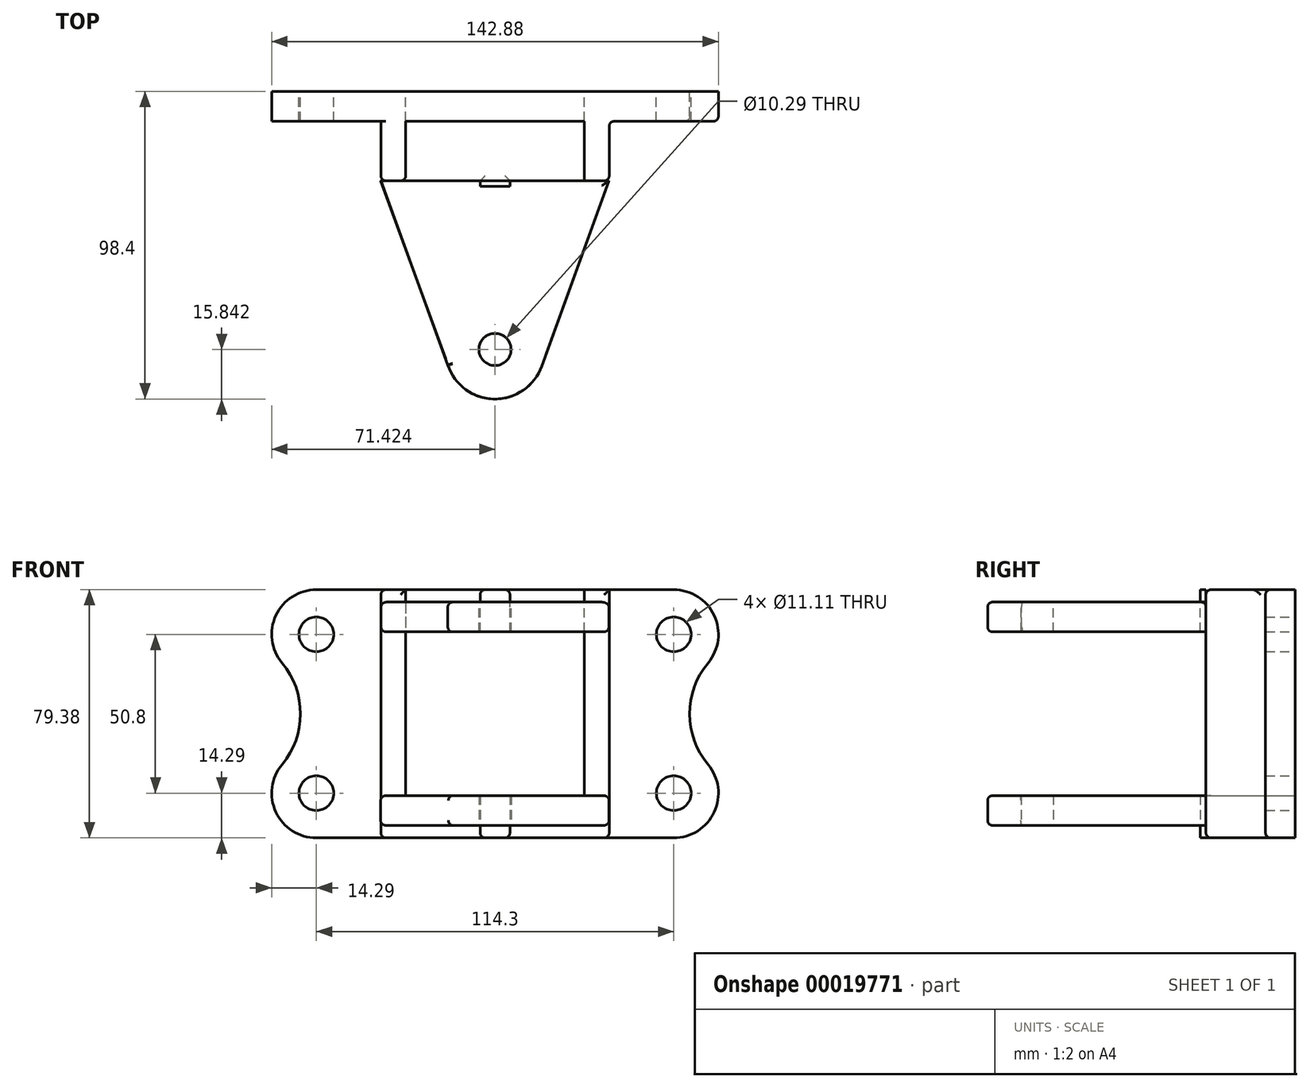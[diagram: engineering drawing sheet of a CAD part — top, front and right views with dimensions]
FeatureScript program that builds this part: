
annotation { "Feature Type Name" : "Feature", "Feature Type Description" : "" }
export const myFeature = defineFeature(function(context is Context, id is Id, definition is map)
    precondition{}
    {
        {
            var Q0;
            Q0=qCreatedBy(makeId("Front.planeOp"),FACE);
            var sketch = newSketch(context, id + "F0", { "sketchPlane" : qUnion([Q0])});
            skLineSegment(sketch, "E0.bottom", {"start": v(16.24, 39.69) * mm, "end": v(73.39, 39.69) * mm});
            skLineSegment(sketch, "E0.top", {"start": v(16.24, -39.69) * mm, "end": v(73.39, -39.69) * mm});
            skLineSegment(sketch, "E1", {"start": v(73.39, 39.69) * mm, "end": v(73.39, 25.4) * mm});
            skArc(sketch, "E2", {"start": v(84.37, 16.26) * mm, "mid": v(86.33, 31.46) * mm, "end": v(73.39, 39.69) * mm});
            skLineSegment(sketch, "E3", {"start": v(73.39, -39.69) * mm, "end": v(73.39, -25.4) * mm});
            skArc(sketch, "E4", {"start": v(73.39, -39.69) * mm, "mid": v(86.33, -31.46) * mm, "end": v(84.37, -16.26) * mm});
            skArc(sketch, "E5", {"start": v(84.37, 16.26) * mm, "mid": v(78.48, 0) * mm, "end": v(84.37, -16.26) * mm});
            skLineSegment(sketch, "E6.trimOffspring", {"start": v(73.39, -11.11) * mm, "end": v(73.39, -39.69) * mm});
            skCircle(sketch, "E7", {"center": v(73.39, 25.4) * mm, "radius": 5.56 * mm});
            skCircle(sketch, "E8", {"center": v(73.39, -25.4) * mm, "radius": 5.56 * mm});
            skLineSegment(sketch, "E9", {"start": v(73.39, 39.69) * mm, "end": v(16.24, 39.69) * mm});
            skLineSegment(sketch, "E10", {"start": v(16.24, 39.69) * mm, "end": v(16.24, 26.2) * mm});
            skLineSegment(sketch, "E11.MirrorCS", {"start": v(-40.91, -39.69) * mm, "end": v(-40.91, -25.4) * mm});
            skLineSegment(sketch, "E12.MirrorCS", {"start": v(16.24, -39.69) * mm, "end": v(-40.91, -39.69) * mm});
            skLineSegment(sketch, "E13.MirrorCS", {"start": v(16.24, 39.69) * mm, "end": v(-40.91, 39.69) * mm});
            skArc(sketch, "E14.MirrorCS", {"start": v(-51.89, 16.26) * mm, "mid": v(-53.85, 31.46) * mm, "end": v(-40.91, 39.69) * mm});
            skLineSegment(sketch, "E15.MirrorCS", {"start": v(-40.91, 39.69) * mm, "end": v(16.24, 39.69) * mm});
            skCircle(sketch, "E16.MirrorC", {"center": v(-40.91, -25.4) * mm, "radius": 5.56 * mm});
            skCircle(sketch, "E17.MirrorC", {"center": v(-40.91, 25.4) * mm, "radius": 5.56 * mm});
            skLineSegment(sketch, "E18.MirrorCS", {"start": v(-40.91, -11.11) * mm, "end": v(-40.91, -39.69) * mm});
            skArc(sketch, "E19.MirrorCS", {"start": v(-51.89, 16.26) * mm, "mid": v(-46, 0) * mm, "end": v(-51.89, -16.26) * mm});
            skArc(sketch, "E20.MirrorCS", {"start": v(-40.91, -39.69) * mm, "mid": v(-53.85, -31.46) * mm, "end": v(-51.89, -16.26) * mm});
            skLineSegment(sketch, "E21.MirrorCS", {"start": v(-40.91, 39.69) * mm, "end": v(-40.91, 25.4) * mm});
            skLineSegment(sketch, "E22", {"start": v(16.24, 26.2) * mm, "end": v(-12.34, 26.2) * mm});
            skLineSegment(sketch, "E23", {"start": v(-12.34, 26.2) * mm, "end": v(-12.34, -26.2) * mm});
            skLineSegment(sketch, "E24", {"start": v(16.24, -26.2) * mm, "end": v(-12.34, -26.2) * mm});
            skLineSegment(sketch, "E25", {"start": v(16.24, -26.2) * mm, "end": v(44.81, -26.2) * mm});
            skLineSegment(sketch, "E26", {"start": v(44.81, -26.2) * mm, "end": v(44.81, 26.2) * mm});
            skLineSegment(sketch, "E27", {"start": v(44.81, 26.2) * mm, "end": v(16.24, 26.2) * mm});
            skPoint(sketch, "E28.end.orphan", {"position": v(-12.34, 0) * mm});
            skLineSegment(sketch, "E29.trimOffspring", {"start": v(16.24, -26.2) * mm, "end": v(16.24, -39.69) * mm});
            skPoint(sketch, "E30.end.orphan", {"position": v(44.81, 0) * mm});
            skPoint(sketch, "E31.start.orphan", {"position": v(16.24, 0) * mm});
            skSolve(sketch);
        }
        {
            var Q0;
            Q0=makeQuery(id+"F0.imprint","IMPRINT",FACE,{"disambiguationData":[TD([[makeQuery(id+"F0.imprint","IMPRINT",EDGE,{"derivedFrom":sQuery(id+"F0.wireOp",EDGE,"E10")}),-1.0]])]});
            var Q1;
            Q1=makeQuery(id+"F0.imprint","IMPRINT",FACE,{"disambiguationData":[TD([[makeQuery(id+"F0.imprint","IMPRINT",EDGE,{"derivedFrom":sQuery(id+"F0.wireOp",EDGE,"E0.top")}),1.0]])]});
            extrude(context, id + "F1", {"entities" : qUnion([Q0, Q1]), "depth" : 9.52 * mm});
        }
        {
            var Q0;
            Q0=makeQuery(id+"F1.opExtrude","CAP_FACE",FACE,{"disambiguationData":[OSD([sQuery(id+"F0.wireOp",EDGE,"E0.top"),sQuery(id+"F0.wireOp",EDGE,"E2"),sQuery(id+"F0.wireOp",EDGE,"E4"),sQuery(id+"F0.wireOp",EDGE,"E5"),sQuery(id+"F0.wireOp",EDGE,"E7"),sQuery(id+"F0.wireOp",EDGE,"E8"),sQuery(id+"F0.wireOp",EDGE,"E9"),sQuery(id+"F0.wireOp",EDGE,"E12.MirrorCS"),sQuery(id+"F0.wireOp",EDGE,"E14.MirrorCS"),sQuery(id+"F0.wireOp",EDGE,"E15.MirrorCS"),sQuery(id+"F0.wireOp",EDGE,"E16.MirrorC"),sQuery(id+"F0.wireOp",EDGE,"E17.MirrorC"),sQuery(id+"F0.wireOp",EDGE,"E19.MirrorCS"),sQuery(id+"F0.wireOp",EDGE,"E20.MirrorCS"),sQuery(id+"F0.wireOp",EDGE,"E22"),sQuery(id+"F0.wireOp",EDGE,"E23"),sQuery(id+"F0.wireOp",EDGE,"E24"),sQuery(id+"F0.wireOp",EDGE,"E25"),sQuery(id+"F0.wireOp",EDGE,"E26"),sQuery(id+"F0.wireOp",EDGE,"E27")])],"isStart":false});
            var sketch = newSketch(context, id + "F2", { "sketchPlane" : qUnion([Q0])});
            skLineSegment(sketch, "E32", {"start": v(-20.27, 39.69) * mm, "end": v(-20.27, -39.69) * mm});
            skLineSegment(sketch, "E33", {"start": v(-20.27, -39.69) * mm, "end": v(-12.34, -39.69) * mm});
            skLineSegment(sketch, "E34", {"start": v(-12.34, -39.69) * mm, "end": v(-12.34, 39.69) * mm});
            skLineSegment(sketch, "E35", {"start": v(-12.34, 39.69) * mm, "end": v(-20.27, 39.69) * mm});
            skLineSegment(sketch, "E36", {"start": v(44.81, 26.2) * mm, "end": v(44.81, 39.69) * mm});
            skLineSegment(sketch, "E37", {"start": v(44.81, 39.69) * mm, "end": v(44.81, -39.69) * mm});
            skLineSegment(sketch, "E38", {"start": v(44.81, -39.69) * mm, "end": v(52.75, -39.69) * mm});
            skLineSegment(sketch, "E39", {"start": v(52.75, -39.69) * mm, "end": v(52.75, 39.69) * mm});
            skLineSegment(sketch, "E40", {"start": v(52.75, 39.69) * mm, "end": v(44.81, 39.69) * mm});
            skLineSegment(sketch, "E41", {"start": v(-12.34, 39.69) * mm, "end": v(44.81, 39.69) * mm});
            skLineSegment(sketch, "E42", {"start": v(-12.34, 26.2) * mm, "end": v(44.81, 26.2) * mm});
            skLineSegment(sketch, "E43", {"start": v(-12.34, -26.2) * mm, "end": v(44.81, -26.2) * mm});
            skLineSegment(sketch, "E44", {"start": v(44.81, -26.2) * mm, "end": v(44.81, 26.2) * mm});
            skLineSegment(sketch, "E45", {"start": v(44.81, -39.69) * mm, "end": v(-12.34, -39.69) * mm});
            skSolve(sketch);
        }
        {
            var Q0;
            {var subQ1=sQuery(id+"F2.wireOp",EDGE,"E43");Q0=makeQuery(id+"F2.imprint","IMPRINT",FACE,{"disambiguationData":[TD([[makeQuery(id+"F2.imprint","IMPRINT",EDGE,{"derivedFrom":subQ1}),1.0]])]});}
            var Q1;
            Q1=makeQuery(id+"F2.imprint","IMPRINT",FACE,{"disambiguationData":[TD([[makeQuery(id+"F2.imprint","IMPRINT",EDGE,{"derivedFrom":sQuery(id+"F2.wireOp",EDGE,"E32")}),1.0]])]});
            var Q2;
            {var subQ2=sQuery(id+"F2.wireOp",EDGE,"E38");Q2=makeQuery(id+"F2.imprint","IMPRINT",FACE,{"disambiguationData":[TD([[makeQuery(id+"F2.imprint","IMPRINT",EDGE,{"derivedFrom":subQ2}),-1.0]])]});}
            var Q3;
            {var subQ1=sQuery(id+"F2.wireOp",EDGE,"E41");Q3=makeQuery(id+"F2.imprint","IMPRINT",FACE,{"disambiguationData":[TD([[makeQuery(id+"F2.imprint","IMPRINT",EDGE,{"derivedFrom":subQ1}),-1.0]])]});}
            extrude(context, id + "F3", {"entities" : qUnion([Q0, Q1, Q2, Q3]), "operationType" : NewBodyOperationType.ADD, "depth" : 19.05 * mm});
        }
        {
            var Q0;
            Q0=makeQuery(id+"F3.opExtrude","CAP_FACE",FACE,{"disambiguationData":[OSD([sQuery(id+"F2.wireOp",EDGE,"E32"),sQuery(id+"F2.wireOp",EDGE,"E33"),sQuery(id+"F2.wireOp",EDGE,"E34"),sQuery(id+"F2.wireOp",EDGE,"E35"),sQuery(id+"F2.wireOp",EDGE,"E38"),sQuery(id+"F2.wireOp",EDGE,"E39"),sQuery(id+"F2.wireOp",EDGE,"E40"),sQuery(id+"F2.wireOp",EDGE,"E41"),sQuery(id+"F2.wireOp",EDGE,"E42"),sQuery(id+"F2.wireOp",EDGE,"E43"),sQuery(id+"F2.wireOp",EDGE,"E44"),sQuery(id+"F2.wireOp",EDGE,"E45")])],"isStart":false});
            var sketch = newSketch(context, id + "F4", { "sketchPlane" : qUnion([Q0])});
            skLineSegment(sketch, "E46", {"start": v(16.24, -39.69) * mm, "end": v(21, -39.69) * mm});
            skLineSegment(sketch, "E47", {"start": v(16.24, -39.69) * mm, "end": v(11.48, -39.69) * mm});
            skLineSegment(sketch, "E48.bottom", {"start": v(11.48, -39.69) * mm, "end": v(21, -39.69) * mm});
            skLineSegment(sketch, "E48.top", {"start": v(11.48, -35.72) * mm, "end": v(21, -35.72) * mm});
            skLineSegment(sketch, "E48.left", {"start": v(11.48, -39.69) * mm, "end": v(11.48, -35.72) * mm});
            skLineSegment(sketch, "E48.right", {"start": v(21, -39.69) * mm, "end": v(21, -35.72) * mm});
            skLineSegment(sketch, "E49", {"start": v(11.48, 39.69) * mm, "end": v(21, 39.69) * mm});
            skLineSegment(sketch, "E50", {"start": v(21, 35.72) * mm, "end": v(11.48, 35.72) * mm});
            skLineSegment(sketch, "E51", {"start": v(11.48, 35.72) * mm, "end": v(11.48, 39.69) * mm});
            skLineSegment(sketch, "E52", {"start": v(21, 39.69) * mm, "end": v(21, 35.72) * mm});
            skPoint(sketch, "E53.orphan", {"position": v(22.57, 35.72) * mm});
            skSolve(sketch);
        }
        {
            var Q0;
            Q0=makeQuery(id+"F4.imprint","IMPRINT",FACE,{"disambiguationData":[TD([[makeQuery(id+"F4.imprint","IMPRINT",EDGE,{"derivedFrom":sQuery(id+"F4.wireOp",EDGE,"E49")}),-1.0]])]});
            var Q1;
            Q1=makeQuery(id+"F4.imprint","IMPRINT",FACE,{"disambiguationData":[TD([[makeQuery(id+"F4.imprint","IMPRINT",EDGE,{"derivedFrom":sQuery(id+"F4.wireOp",EDGE,"E48.top")}),-1.0]])]});
            extrude(context, id + "F5", {"entities" : qUnion([Q0, Q1]), "operationType" : NewBodyOperationType.ADD, "depth" : (2.12 - (11 / 32)) * mm});
        }
        {
            var Q0;
            Q0=makeQuery(id+"F5.opExtrude","SWEPT_FACE",FACE,{"disambiguationData":[OSD([sQuery(id+"F4.wireOp",EDGE,"E48.top")])]});
            var sketch = newSketch(context, id + "F6", { "sketchPlane" : qUnion([Q0])});
            skSolve(sketch);
        }
        {
            var Q0;
            Q0=makeQuery(id+"F5.opExtrude","SWEPT_FACE",FACE,{"disambiguationData":[OSD([sQuery(id+"F4.wireOp",EDGE,"E50")])]});
            var sketch = newSketch(context, id + "F7", { "sketchPlane" : qUnion([Q0])});
            skLineSegment(sketch, "E54", {"start": v(-20.22, 28.6) * mm, "end": v(52.63, 28.58) * mm});
            skLineSegment(sketch, "E55", {"start": v(52.63, 28.57) * mm, "end": v(31.17, 87.84) * mm});
            skLineSegment(sketch, "E56", {"start": v(-20.22, 28.6) * mm, "end": v(1.32, 87.97) * mm});
            skCircle(sketch, "E57", {"center": v(16.22, 82.54) * mm, "radius": 5.14 * mm});
            skArc(sketch, "E58", {"start": v(31.17, 87.84) * mm, "mid": v(16.03, 98.4) * mm, "end": v(1.15, 87.48) * mm});
            skSolve(sketch);
        }
        {
            var Q0;
            {var subQ10=sQuery(id+"F7.wireOp",EDGE,"E55");Q0=makeQuery(id+"F7.imprint","IMPRINT",FACE,{"disambiguationData":[TD([[makeQuery(id+"F7.imprint","IMPRINT",EDGE,{"derivedFrom":subQ10}),1.0]])]});}
            extrude(context, id + "F8", {"entities" : qUnion([Q0]), "depth" : 9.52 * mm});
        }
        {
            var Q0;
            Q0=makeQuery(id+"F5.opExtrude","SWEPT_FACE",FACE,{"disambiguationData":[OSD([sQuery(id+"F4.wireOp",EDGE,"E50")])]});
            extrude(context, id + "F9", {"entities" : qUnion([Q0]), "depth" : 9.52 * mm});
        }
        {
            var Q0;
            {var subQ0=sQuery(id+"F4.wireOp",EDGE,"E48.top");Q0=makeQuery(id+"F6.imprint","IMPRINT",FACE,{"disambiguationData":[TD([[makeQuery(id+"F6.imprint","IMPRINT",EDGE,{"derivedFrom":makeQuery(id+"F5.opExtrude","CAP_EDGE",EDGE,{"disambiguationData":[OSD([subQ0])],"isStart":false})}),1.0]])]});}
            var sketch = newSketch(context, id + "F10", { "sketchPlane" : qUnion([Q0])});
            skLineSegment(sketch, "E59", {"start": v(-20.35, -28.64) * mm, "end": v(52.69, -28.64) * mm});
            skLineSegment(sketch, "E60", {"start": v(52.69, -28.64) * mm, "end": v(31.12, -87.97) * mm});
            skLineSegment(sketch, "E61", {"start": v(-20.35, -28.64) * mm, "end": v(1.33, -87.96) * mm});
            skCircle(sketch, "E62", {"center": v(16.22, -82.56) * mm, "radius": 5.15 * mm});
            skArc(sketch, "E63", {"start": v(1.3, -87.87) * mm, "mid": v(16.17, -98.4) * mm, "end": v(31.12, -87.97) * mm});
            skSolve(sketch);
        }
        {
            var Q0;
            {var subQ10=sQuery(id+"F10.wireOp",EDGE,"E60");Q0=makeQuery(id+"F10.imprint","IMPRINT",FACE,{"disambiguationData":[TD([[makeQuery(id+"F10.imprint","IMPRINT",EDGE,{"derivedFrom":subQ10}),-1.0]])]});}
            extrude(context, id + "F11", {"entities" : qUnion([Q0]), "depth" : 9.52 * mm});
        }
        {
            var Q0;
            {var subQ0=sQuery(id+"F4.wireOp",EDGE,"E48.top");Q0=makeQuery(id+"F6.imprint","IMPRINT",FACE,{"disambiguationData":[TD([[makeQuery(id+"F6.imprint","IMPRINT",EDGE,{"derivedFrom":makeQuery(id+"F5.opExtrude","CAP_EDGE",EDGE,{"disambiguationData":[OSD([subQ0])],"isStart":false})}),1.0]])]});}
            extrude(context, id + "F12", {"entities" : qUnion([Q0]), "depth" : 9.52 * mm});
        }
        {
            var Q0;
            Q0=makeQuery(id+"F5.opExtrude","SWEPT_EDGE",EDGE,{"disambiguationData":[OSD([sQuery(id+"F2.wireOp",EDGE,"E33"),sQuery(id+"F2.wireOp",EDGE,"E38"),sQuery(id+"F2.wireOp",EDGE,"E45"),sQuery(id+"F4.wireOp",EDGE,"E48.bottom"),sQuery(id+"F4.wireOp",EDGE,"E48.left")])]});
            var Q1;
            Q1=makeQuery(id+"F5.opExtrude","SWEPT_EDGE",EDGE,{"disambiguationData":[OSD([sQuery(id+"F2.wireOp",EDGE,"E33"),sQuery(id+"F2.wireOp",EDGE,"E38"),sQuery(id+"F2.wireOp",EDGE,"E45"),sQuery(id+"F4.wireOp",EDGE,"E48.bottom"),sQuery(id+"F4.wireOp",EDGE,"E48.right")])]});
            var Q2;
            {var subQ0=sQuery(id+"F2.wireOp",EDGE,"E33");var subQ1=sQuery(id+"F2.wireOp",EDGE,"E38");var subQ2=sQuery(id+"F2.wireOp",EDGE,"E45");var subQ3=sQuery(id+"F2.wireOp",EDGE,"E32");Q2=makeQuery(id+"F5.boolean.opBoolean","SPLIT",EDGE,{"disambiguationData":[TD([makeQuery(id+"F3.opExtrude","SWEPT_FACE",FACE,{"disambiguationData":[OSD([subQ3])]})])],"derivedFrom":makeQuery(id+"F3.opExtrude","CAP_EDGE",EDGE,{"disambiguationData":[OSD([subQ0,subQ1,subQ2])],"isStart":false})});}
            var Q3;
            {var subQ0=sQuery(id+"F2.wireOp",EDGE,"E33");var subQ1=sQuery(id+"F2.wireOp",EDGE,"E38");var subQ2=sQuery(id+"F2.wireOp",EDGE,"E45");var subQ3=sQuery(id+"F2.wireOp",EDGE,"E39");Q3=makeQuery(id+"F5.boolean.opBoolean","SPLIT",EDGE,{"disambiguationData":[TD([makeQuery(id+"F3.opExtrude","SWEPT_FACE",FACE,{"disambiguationData":[OSD([subQ3])]})])],"derivedFrom":makeQuery(id+"F3.opExtrude","CAP_EDGE",EDGE,{"disambiguationData":[OSD([subQ0,subQ1,subQ2])],"isStart":false})});}
            var Q4;
            Q4=makeQuery(id+"F11.opExtrude","CAP_EDGE",EDGE,{"disambiguationData":[OSD([sQuery(id+"F10.wireOp",EDGE,"E61")])],"isStart":true});
            var Q5;
            Q5=makeQuery(id+"F11.opExtrude","CAP_EDGE",EDGE,{"disambiguationData":[OSD([sQuery(id+"F10.wireOp",EDGE,"E63")])],"isStart":true});
            var Q6;
            Q6=makeQuery(id+"F3.opExtrude","SWEPT_EDGE",EDGE,{"disambiguationData":[OSD([sQuery(id+"F0.wireOp",EDGE,"E0.top"),sQuery(id+"F0.wireOp",EDGE,"E12.MirrorCS"),sQuery(id+"F2.wireOp",EDGE,"E32"),sQuery(id+"F2.wireOp",EDGE,"E33")])]});
            var Q7;
            Q7=makeQuery(id+"F3.opExtrude","CAP_EDGE",EDGE,{"disambiguationData":[OSD([sQuery(id+"F2.wireOp",EDGE,"E32")])],"isStart":false});
            var Q8;
            Q8=makeQuery(id+"F3.opExtrude","SWEPT_EDGE",EDGE,{"disambiguationData":[OSD([sQuery(id+"F0.wireOp",EDGE,"E9"),sQuery(id+"F0.wireOp",EDGE,"E15.MirrorCS"),sQuery(id+"F2.wireOp",EDGE,"E32"),sQuery(id+"F2.wireOp",EDGE,"E35")])]});
            var Q9;
            Q9=makeQuery(id+"F3.opExtrude","CAP_EDGE",EDGE,{"disambiguationData":[OSD([sQuery(id+"F2.wireOp",EDGE,"E32")])],"isStart":true});
            var Q10;
            Q10=makeQuery(id+"F3.opExtrude","SWEPT_EDGE",EDGE,{"disambiguationData":[OSD([sQuery(id+"F0.wireOp",EDGE,"E0.top"),sQuery(id+"F0.wireOp",EDGE,"E12.MirrorCS"),sQuery(id+"F2.wireOp",EDGE,"E38"),sQuery(id+"F2.wireOp",EDGE,"E39")])]});
            var Q11;
            Q11=makeQuery(id+"F3.opExtrude","CAP_EDGE",EDGE,{"disambiguationData":[OSD([sQuery(id+"F2.wireOp",EDGE,"E39")])],"isStart":false});
            var Q12;
            Q12=makeQuery(id+"F3.opExtrude","CAP_EDGE",EDGE,{"disambiguationData":[OSD([sQuery(id+"F2.wireOp",EDGE,"E39")])],"isStart":true});
            var Q13;
            {var subQ0=sQuery(id+"F0.wireOp",EDGE,"E0.top");var subQ1=sQuery(id+"F0.wireOp",EDGE,"E12.MirrorCS");var subQ2=sQuery(id+"F0.wireOp",EDGE,"E4");Q13=makeQuery(id+"F3.boolean.opBoolean","SPLIT",EDGE,{"disambiguationData":[TD([makeQuery(id+"F1.opExtrude","SWEPT_FACE",FACE,{"disambiguationData":[OSD([subQ2])]})])],"derivedFrom":makeQuery(id+"F1.opExtrude","CAP_EDGE",EDGE,{"disambiguationData":[OSD([subQ0,subQ1])],"isStart":false})});}
            var Q14;
            Q14=makeQuery(id+"F11.opExtrude","CAP_EDGE",EDGE,{"disambiguationData":[OSD([sQuery(id+"F10.wireOp",EDGE,"E60")])],"isStart":false});
            var Q15;
            Q15=makeQuery(id+"F11.opExtrude","CAP_EDGE",EDGE,{"disambiguationData":[OSD([sQuery(id+"F10.wireOp",EDGE,"E63")])],"isStart":false});
            var Q16;
            Q16=makeQuery(id+"F8.opExtrude","CAP_EDGE",EDGE,{"disambiguationData":[OSD([sQuery(id+"F7.wireOp",EDGE,"E55")])],"isStart":false});
            var Q17;
            Q17=makeQuery(id+"F8.opExtrude","CAP_EDGE",EDGE,{"disambiguationData":[OSD([sQuery(id+"F7.wireOp",EDGE,"E58")])],"isStart":false});
            var Q18;
            Q18=makeQuery(id+"F8.opExtrude","CAP_EDGE",EDGE,{"disambiguationData":[OSD([sQuery(id+"F7.wireOp",EDGE,"E56")])],"isStart":false});
            var Q19;
            Q19=makeQuery(id+"F8.opExtrude","CAP_EDGE",EDGE,{"disambiguationData":[OSD([sQuery(id+"F7.wireOp",EDGE,"E55")])],"isStart":true});
            var Q20;
            Q20=makeQuery(id+"F8.opExtrude","CAP_EDGE",EDGE,{"disambiguationData":[OSD([sQuery(id+"F7.wireOp",EDGE,"E56")])],"isStart":true});
            var Q21;
            Q21=makeQuery(id+"F8.opExtrude","CAP_EDGE",EDGE,{"disambiguationData":[OSD([sQuery(id+"F7.wireOp",EDGE,"E58")])],"isStart":true});
            var Q22;
            {var subQ0=sQuery(id+"F2.wireOp",EDGE,"E35");var subQ1=sQuery(id+"F2.wireOp",EDGE,"E40");var subQ2=sQuery(id+"F2.wireOp",EDGE,"E41");var subQ3=sQuery(id+"F2.wireOp",EDGE,"E39");Q22=makeQuery(id+"F5.boolean.opBoolean","SPLIT",EDGE,{"disambiguationData":[TD([makeQuery(id+"F3.opExtrude","SWEPT_FACE",FACE,{"disambiguationData":[OSD([subQ3])]})])],"derivedFrom":makeQuery(id+"F3.opExtrude","CAP_EDGE",EDGE,{"disambiguationData":[OSD([subQ0,subQ1,subQ2])],"isStart":false})});}
            var Q23;
            {var subQ0=sQuery(id+"F7.wireOp",EDGE,"E54");Q23=makeQuery(id+"F8.opExtrude","CAP_EDGE",EDGE,{"disambiguationData":[OSD([subQ0]),TDD([makeQuery(id+"F7.imprint","IMPRINT",EDGE,{"disambiguationData":[TD([[makeQuery(id+"F7.imprint","INTERSECT",VERTEX,{"derivedFrom":[subQ0,sQuery(id+"F7.wireOp",EDGE,"E55")]}),1.0]])],"derivedFrom":subQ0})])],"isStart":true});}
            var Q24;
            Q24=makeQuery(id+"F5.opExtrude","SWEPT_EDGE",EDGE,{"disambiguationData":[OSD([sQuery(id+"F2.wireOp",EDGE,"E35"),sQuery(id+"F2.wireOp",EDGE,"E40"),sQuery(id+"F2.wireOp",EDGE,"E41"),sQuery(id+"F4.wireOp",EDGE,"E49"),sQuery(id+"F4.wireOp",EDGE,"E52")])]});
            var Q25;
            Q25=makeQuery(id+"F5.opExtrude","SWEPT_EDGE",EDGE,{"disambiguationData":[OSD([sQuery(id+"F2.wireOp",EDGE,"E35"),sQuery(id+"F2.wireOp",EDGE,"E40"),sQuery(id+"F2.wireOp",EDGE,"E41"),sQuery(id+"F4.wireOp",EDGE,"E49"),sQuery(id+"F4.wireOp",EDGE,"E51")])]});
            var Q26;
            {var subQ0=sQuery(id+"F2.wireOp",EDGE,"E35");var subQ1=sQuery(id+"F2.wireOp",EDGE,"E40");var subQ2=sQuery(id+"F2.wireOp",EDGE,"E41");var subQ3=sQuery(id+"F2.wireOp",EDGE,"E32");Q26=makeQuery(id+"F5.boolean.opBoolean","SPLIT",EDGE,{"disambiguationData":[TD([makeQuery(id+"F3.opExtrude","SWEPT_FACE",FACE,{"disambiguationData":[OSD([subQ3])]})])],"derivedFrom":makeQuery(id+"F3.opExtrude","CAP_EDGE",EDGE,{"disambiguationData":[OSD([subQ0,subQ1,subQ2])],"isStart":false})});}
            var Q27;
            Q27=makeQuery(id+"F3.opExtrude","CAP_EDGE",EDGE,{"disambiguationData":[OSD([sQuery(id+"F2.wireOp",EDGE,"E34")])],"isStart":false});
            var Q28;
            Q28=makeQuery(id+"F3.opExtrude","CAP_EDGE",EDGE,{"disambiguationData":[OSD([sQuery(id+"F2.wireOp",EDGE,"E44")])],"isStart":false});
            fillet(context, id + "F13", {"entities" : qUnion([Q0, Q1, Q2, Q3, Q4, Q5, Q6, Q7, Q8, Q9, Q10, Q11, Q12, Q13, Q14, Q15, Q16, Q17, Q18, Q19, Q20, Q21, Q22, Q23, Q24, Q25, Q26, Q27, Q28]), "radius" : 1.59 * mm, "tangentPropagation" : true, "allowEdgeOverflow" : false});
        }
    });
